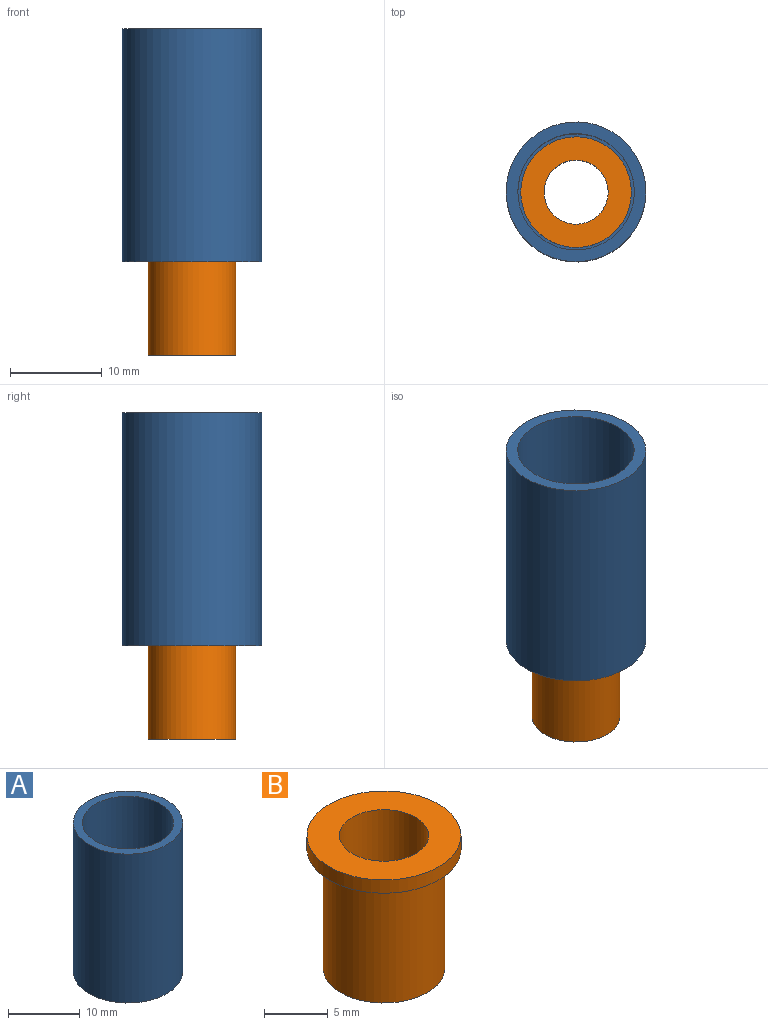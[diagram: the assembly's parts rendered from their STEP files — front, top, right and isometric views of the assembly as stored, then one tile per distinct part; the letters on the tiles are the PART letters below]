
ASSEMBLY  parts=2 mates=1
PART A: 6 faces, bbox 15.2x15.2x25.4 mm
  f0: plane 12.7x12.7mm, normal (0,0,1), area 45.6mm2, adj f1,f5
  f1: cylinder r=5.08mm len=10.16mm, axis (0,0,-1), area 40.5mm2, adj f0,f2
  f2: plane 15.24x15.24mm, normal (0,0,-1), area 101.3mm2, adj f1,f3
  f3: cylinder r=7.62mm len=25.4mm, axis (0,0,-1), area 1216.1mm2, adj f2,f4
  f4: plane 15.24x15.24mm, normal (0,0,1), area 55.7mm2, adj f3,f5
  f5: cylinder r=6.35mm len=24.13mm, axis (0,0,-1), area 962.7mm2, adj f0,f4
PART B: 11 faces, bbox 12.1x12.1x12.7 mm
  f0: plane 9.53x9.53mm, normal (0,0,-1), area 32.9mm2, adj f1,f10
  f1: cylinder r=4.76mm len=11.43mm, axis (0,0,-1), area 342mm2, adj f0,f2
  f2: plane 12.07x12.07mm, normal (0,0,-1), area 43.1mm2, adj f1,f3
  f3: cylinder r=6.03mm len=12.07mm, axis (0,0,-1), area 48.1mm2, adj f2,f4
  f4: plane 12.07x12.07mm, normal (0,0,1), area 76mm2, adj f3,f5
  f5: cylinder r=3.49mm len=6.99mm, axis (0,0,-1), area 111.5mm2, adj f4,f6
  f6: cone r=3.49mm half-angle=45deg, axis (0,0,-1), area 21.5mm2, adj f5,f7
  f7: cone r=4.13mm half-angle=45deg, axis (0,0,1), area 21.5mm2, adj f6,f8
  f8: cone r=3.49mm half-angle=45deg, axis (0,0,-1), area 21.5mm2, adj f7,f9
  f9: cone r=4.13mm half-angle=45deg, axis (0,0,1), area 21.5mm2, adj f8,f10
  f10: cylinder r=3.49mm len=6.99mm, axis (0,0,-1), area 111.5mm2, adj f0,f9
PLACE A t=(-10.53,-9.12,-0.77)mm fixed
PLACE B t=(-10.53,-9.12,-10.97)mm
MATE slider B.f1 <-> A.f1  axis (0,0,-1) through (-10.53,-9.12,-8.43)mm
